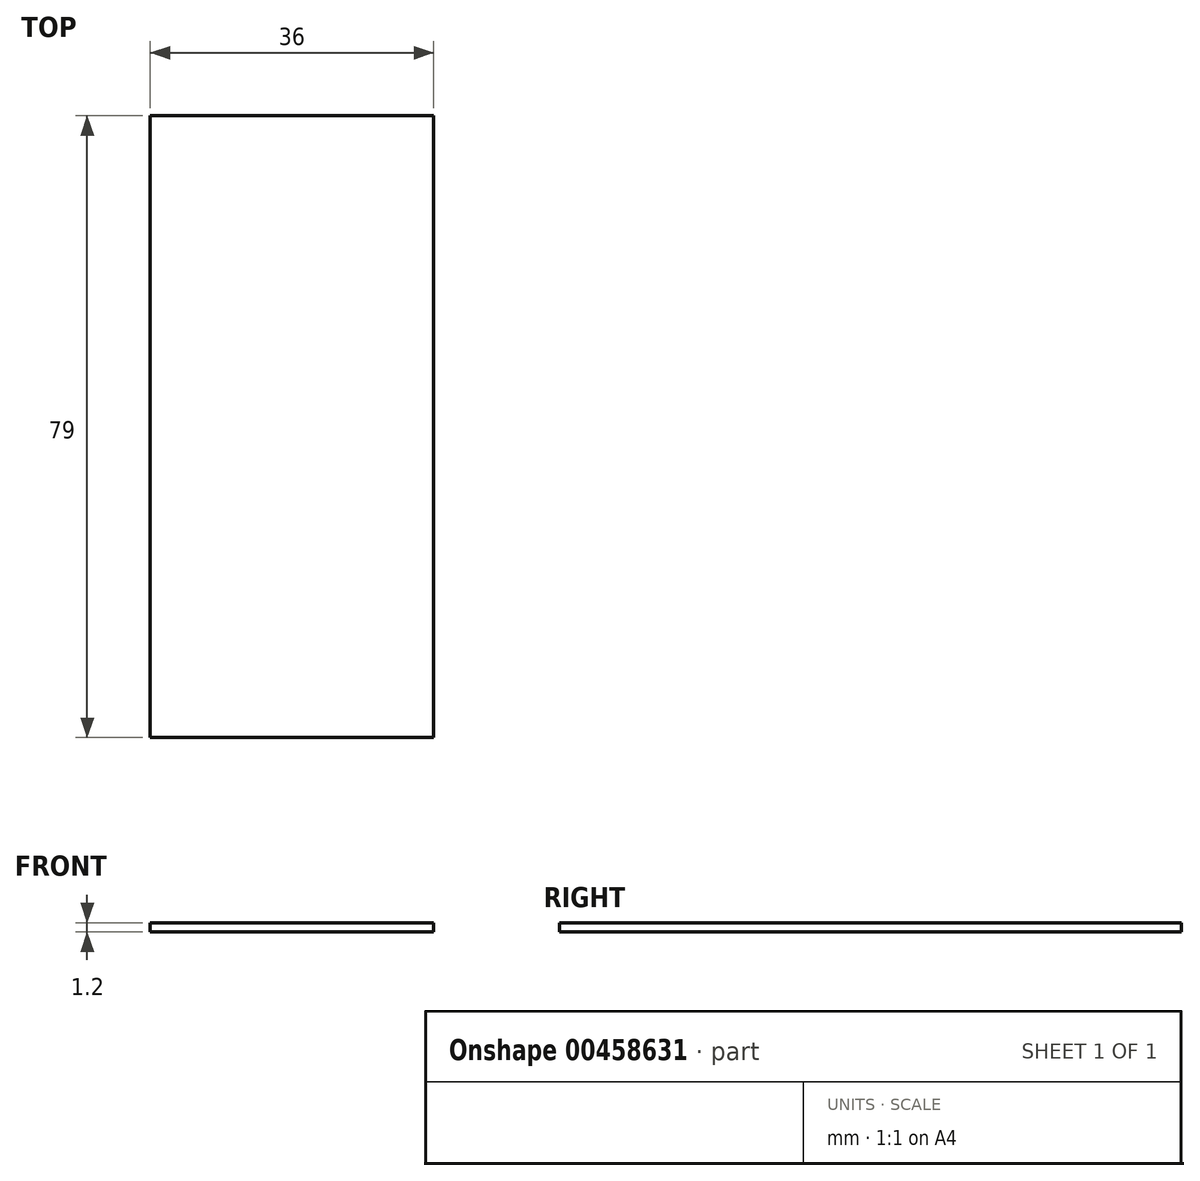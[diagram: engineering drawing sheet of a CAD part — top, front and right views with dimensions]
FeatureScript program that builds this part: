
annotation { "Feature Type Name" : "Feature", "Feature Type Description" : "" }
export const myFeature = defineFeature(function(context is Context, id is Id, definition is map)
    precondition{}
    {
        {
            var Q0;
            Q0=qCreatedBy(makeId("Top.planeOp"),FACE);
            var sketch = newSketch(context, id + "F0", { "sketchPlane" : qUnion([Q0])});
            skLineSegment(sketch, "E0.bottom", {"start": v(18.86, 37.5) * mm, "end": v(-13.14, 37.5) * mm});
            skLineSegment(sketch, "E0.top", {"start": v(18.86, -37.5) * mm, "end": v(-13.14, -37.5) * mm});
            skLineSegment(sketch, "E0.left", {"start": v(18.86, 37.5) * mm, "end": v(18.86, -37.5) * mm});
            skLineSegment(sketch, "E0.right", {"start": v(-13.14, 37.5) * mm, "end": v(-13.14, -37.5) * mm});
            skPoint(sketch, "E0.middle", {"position": v(2.86, 0) * mm});
            skLineSegment(sketch, "E1.0", {"start": v(20.86, 39.5) * mm, "end": v(-15.14, 39.5) * mm});
            skLineSegment(sketch, "E1.1", {"start": v(20.86, 39.5) * mm, "end": v(20.86, -39.5) * mm});
            skLineSegment(sketch, "E1.2", {"start": v(20.86, -39.5) * mm, "end": v(-15.14, -39.5) * mm});
            skLineSegment(sketch, "E1.3", {"start": v(-15.14, 39.5) * mm, "end": v(-15.14, -39.5) * mm});
            skCircle(sketch, "E2", {"center": v(-7.14, 25) * mm, "radius": 1.5 * mm});
            skCircle(sketch, "E3.MirrorC", {"center": v(-7.14, -25) * mm, "radius": 1.5 * mm});
            skLineSegment(sketch, "E4", {"start": v(2.86, -37.5) * mm, "end": v(2.86, 37.5) * mm});
            skCircle(sketch, "E5", {"center": v(-7.14, 25) * mm, "radius": 3 * mm});
            skCircle(sketch, "E6.MirrorC", {"center": v(-7.14, -25) * mm, "radius": 3 * mm});
            skSolve(sketch);
        }
        {
            var Q0;
            {var subQ4=sQuery(id+"F0.wireOp",EDGE,"E0.left");Q0=makeQuery(id+"F0.imprint","IMPRINT",FACE,{"disambiguationData":[TD([[makeQuery(id+"F0.imprint","IMPRINT",EDGE,{"derivedFrom":subQ4}),1.0]])]});}
            var Q1;
            {var subQ1=sQuery(id+"F0.wireOp",EDGE,"E0.right");Q1=makeQuery(id+"F0.imprint","IMPRINT",FACE,{"disambiguationData":[TD([[makeQuery(id+"F0.imprint","IMPRINT",EDGE,{"derivedFrom":subQ1}),1.0]])]});}
            var Q2;
            Q2=makeQuery(id+"F0.imprint","IMPRINT",FACE,{"disambiguationData":[TD([[makeQuery(id+"F0.imprint","IMPRINT",EDGE,{"derivedFrom":sQuery(id+"F0.wireOp",EDGE,"E2")}),1.0]])]});
            var Q3;
            Q3=makeQuery(id+"F0.imprint","IMPRINT",FACE,{"disambiguationData":[TD([[makeQuery(id+"F0.imprint","IMPRINT",EDGE,{"derivedFrom":sQuery(id+"F0.wireOp",EDGE,"E2")}),-1.0]])]});
            var Q4;
            Q4=makeQuery(id+"F0.imprint","IMPRINT",FACE,{"disambiguationData":[TD([[makeQuery(id+"F0.imprint","IMPRINT",EDGE,{"derivedFrom":sQuery(id+"F0.wireOp",EDGE,"E3.MirrorC")}),1.0]])]});
            var Q5;
            Q5=makeQuery(id+"F0.imprint","IMPRINT",FACE,{"disambiguationData":[TD([[makeQuery(id+"F0.imprint","IMPRINT",EDGE,{"derivedFrom":sQuery(id+"F0.wireOp",EDGE,"E3.MirrorC")}),-1.0]])]});
            var Q6;
            {var subQ0=sQuery(id+"F0.wireOp",EDGE,"E0.left");Q6=makeQuery(id+"F0.imprint","IMPRINT",FACE,{"disambiguationData":[TD([[makeQuery(id+"F0.imprint","IMPRINT",EDGE,{"derivedFrom":subQ0}),-1.0]])]});}
            extrude(context, id + "F1", {"entities" : qUnion([Q0, Q1, Q2, Q3, Q4, Q5, Q6]), "depth" : 1.2 * mm});
        }
    });
